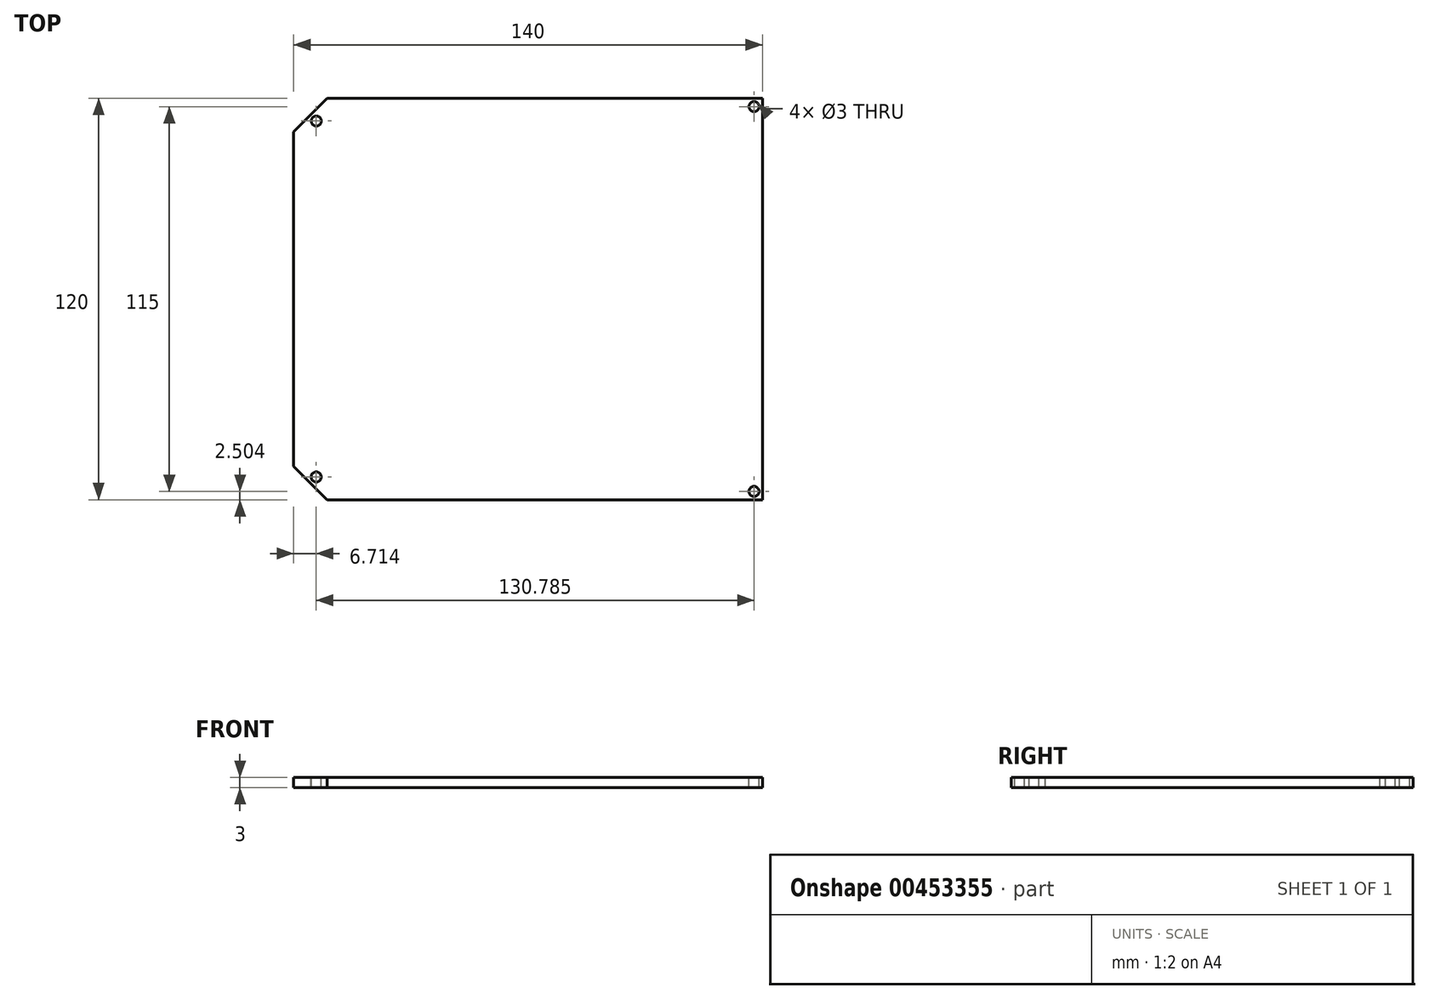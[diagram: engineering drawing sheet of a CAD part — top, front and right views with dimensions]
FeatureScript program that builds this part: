
annotation { "Feature Type Name" : "Feature", "Feature Type Description" : "" }
export const myFeature = defineFeature(function(context is Context, id is Id, definition is map)
    precondition{}
    {
        {
            var Q0;
            Q0=qCreatedBy(makeId("Top.planeOp"),FACE);
            var sketch = newSketch(context, id + "F0", { "sketchPlane" : qUnion([Q0])});
            skLineSegment(sketch, "E0", {"start": v(-6.1, -12.08) * mm, "end": v(-6.1, -183.87) * mm, "construction": true});
            skLineSegment(sketch, "E1", {"start": v(-6.1, -183.87) * mm, "end": v(-6.1, 190.39) * mm, "construction": true});
            skLineSegment(sketch, "E2", {"start": v(-6.1, -12.08) * mm, "end": v(523.09, -12.08) * mm, "construction": true});
            skLineSegment(sketch, "E3", {"start": v(523.09, -12.08) * mm, "end": v(-453, -12.08) * mm, "construction": true});
            skLineSegment(sketch, "E4.bottom", {"start": v(63.9, 47.92) * mm, "end": v(-66.1, 47.92) * mm});
            skLineSegment(sketch, "E4.top", {"start": v(63.9, -72.08) * mm, "end": v(-66.1, -72.08) * mm});
            skLineSegment(sketch, "E4.left", {"start": v(63.9, 47.92) * mm, "end": v(63.9, -72.08) * mm});
            skLineSegment(sketch, "E4.right", {"start": v(-76.1, 37.92) * mm, "end": v(-76.1, -62.08) * mm});
            skPoint(sketch, "E4.middle", {"position": v(-6.1, -12.08) * mm});
            skLineSegment(sketch, "E5.MirrorCS", {"start": v(63.9, 47.92) * mm, "end": v(63.9, 167.92) * mm});
            skLineSegment(sketch, "E6.MirrorCS", {"start": v(63.9, 167.92) * mm, "end": v(-76.1, 167.92) * mm});
            skLineSegment(sketch, "E7", {"start": v(-76.1, -62.08) * mm, "end": v(-66.1, -72.08) * mm});
            skLineSegment(sketch, "E8.MirrorCS", {"start": v(-76.1, 37.92) * mm, "end": v(-66.1, 47.92) * mm});
            skPoint(sketch, "E9.orphan", {"position": v(-76.1, 47.92) * mm});
            skPoint(sketch, "E10.orphan", {"position": v(-76.1, -72.08) * mm});
            skSolve(sketch);
        }
        {
            var Q0;
            Q0 = qSketchRegion(id + "F0", true);
            extrude(context, id + "F1", {"entities" : qUnion([Q0]), "depth" : 3 * mm});
        }
        {
            var Q0;
            Q0=makeQuery(id+"F1.opExtrude","CAP_FACE",FACE,{"disambiguationData":[OSD([sQuery(id+"F0.wireOp",EDGE,"E4.bottom"),sQuery(id+"F0.wireOp",EDGE,"E4.top"),sQuery(id+"F0.wireOp",EDGE,"E4.left"),sQuery(id+"F0.wireOp",EDGE,"E4.right"),sQuery(id+"F0.wireOp",EDGE,"E7"),sQuery(id+"F0.wireOp",EDGE,"E8.MirrorCS")])],"isStart":false});
            var sketch = newSketch(context, id + "F2", { "sketchPlane" : qUnion([Q0])});
            skCircle(sketch, "E11", {"center": v(61.4, 45.42) * mm, "radius": 1.5 * mm});
            skCircle(sketch, "E12", {"center": v(61.4, -69.58) * mm, "radius": 1.5 * mm});
            skCircle(sketch, "E13", {"center": v(-69.34, 41.13) * mm, "radius": 1.5 * mm});
            skCircle(sketch, "E14", {"center": v(-69.38, -65.25) * mm, "radius": 1.5 * mm});
            skSolve(sketch);
        }
        {
            var Q0;
            Q0 = qSketchRegion(id + "F2", true);
            extrude(context, id + "F3", {"entities" : qUnion([Q0]), "operationType" : NewBodyOperationType.REMOVE, "oppositeDirection" : true, "depth" : 4 * mm});
        }
    });
